# Revit family: Cameo 2.6
name_source: partatom
category: Lighting Fixtures
revit_build: Autodesk Revit 2017 (Build: 20170419_0315(x64)
units: mm (PartAtom-declared; Revit-internal decimal feet)

## family parameters
Cut with Voids When Loaded = Yes
Host = Face
Light Source = Yes
Part Type = Normal
Room Calculation Point = Yes
Round Connector Dimension = Use Diameter
Shared = No

## types (6) — shared parameters
Apparent Load = 0 VA
Apparent Load Phase 1 = 5 W
Body = L&L_White anodized aluminium
CRI = 90
Code = CM2600100050SN Black; CM2600100050SE White
Color Filter = 16777215
Control system = -
Cutout dimensions = diam. 45 mm
Default Elevation = 1219.2 mm  [stored 4 ft]
Delivered lumen output = 303 lm (3000K, 32°)
Description = Recessed for indoor applications
Dimming Lamp Color Temperature Shift = <None>
Emit from Line Length = 609.6 mm  [stored 2 ft]
Energy efficiency class = A A+ A++
Features = -
Geometry = Cameo2.6_mod
Height Void = 45 mm  [stored 0.147638 ft]
Height mm = 43 mm  [stored 0.141076 ft]
IP = 40
LED Colour = 3000K (also available: 2700K and 4000K - ref. URL Technical sheet)
Length mm = 49 mm  [stored 0.160761 ft]
Lens = L&L_Tempered extra-clear glass
Lumen output at source = 452 lm (3000K)
Manufacturer = L&L Luce&Light
Material = body and trim in aluminium
Model = Cameo 2.6
Mounting = recessed (ceilings, and false ceilings and niches in plasterboard)
No. and type of led = 1 power LED High Intensity, 3-step MacAdam, 50 000h L95 B10 (Ta 25°C)
Notes = -
Power = 5W
Power cables = includes 1.5 m PVC cable FROR 2x0.35/0.35 Ø3.5 m
Power supply = 24Vdc
Power supply unit = not included
Radius Void = 19.5 mm  [stored 0.0639764 ft]
Springs = L&L_C 67 annealed steel
Tilt Angle = 90.00°
Tiltable = -
Trim = L&L_Anodized aluminium
URL = https://www.lucelight.it
URL Accessories and power supply units = https://www.lucelight.it
URL Catalogue = -
URL DXF = https://www.lucelight.it
URL Description = https://www.lucelight.it
URL General code = https://www.lucelight.it
URL IES Photometric file = https://www.lucelight.it
URL Image = https://www.lucelight.it
URL Technical sheet = https://www.lucelight.it
Voltage = 24 V
Weight kg = 0.15 kg
Width mm = 49 mm  [stored 0.160761 ft]
Wiring = parallel

## per-type parameters (varying)
| type | Optics | Photometric Web File |
| Cameo 2.6_J 65° (3000K 5W 24Vdc) | 65° | CAMEO 2.6 J 65° [3000K 5W 24Vdc].IES |
| Cameo 2.6_L 32° (3000K 5W 24Vdc) | 32° | CAMEO 2.6 L 32° [3000K 5W 24Vdc].IES |
| Cameo 2.6_M 17° (3000K 5W 24Vdc) | 17° | CAMEO 2.6 M 17° [3000K 5W 24Vdc].IES |
| Cameo 2.6_P 19° (3000K 5W 24Vdc) | sharp 19° | CAMEO 2.6 P (19°) [3000K 5W 24Vdc].IES |
| Cameo 2.6_S 11° (3000K 5W 24Vdc) | 11° | CAMEO 2.6 S 11° [3000K 5W 24Vdc].IES |
| Cameo 2.6_W 13°x43° (3000K 5W 24Vdc) | 13°x43° | CAMEO 2.6 W 13°x43° [3000K 5W 24Vdc].IES |

note: [stored X ft] marks values corroborated as IEEE doubles in the binary element streams (Revit-internal decimal feet)

## geometry (parser evidence)
native form markers: Blend x2, Sweep x4
no freeform markers — native parametric forms only
